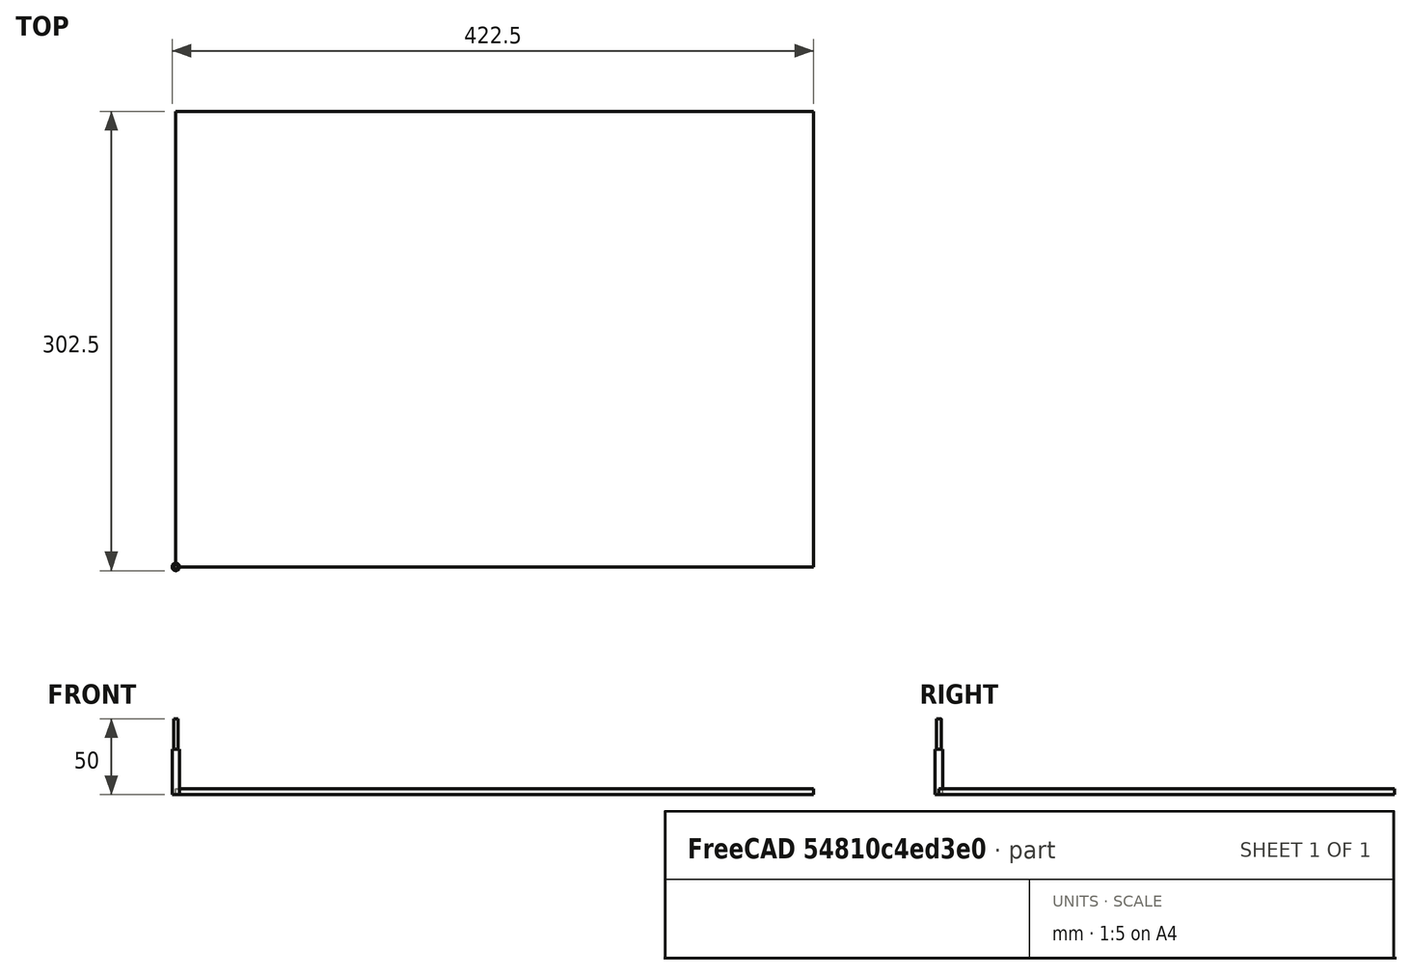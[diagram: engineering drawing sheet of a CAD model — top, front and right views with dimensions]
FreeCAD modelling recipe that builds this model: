
FCSTD DOCUMENT  (FreeCAD 0.21R33771 (Git))
Label: HousingAtari_Level_2_T01
License: All rights reserved
LicenseURL: https://en.wikipedia.org/wiki/All_rights_reserved
objects: Sketcher::SketchObject×7, Part::Part2DObjectPython×5, TechDraw::DrawViewDraft×4, Path::FeaturePython×3, App::DocumentObjectGroup×3, Part::FeaturePython×2, PartDesign::Body×1, App::FeaturePython×1, Mesh::FeaturePython×1, TechDraw::DrawSVGTemplate×1, TechDraw::DrawPage×1
note: 15 computed .brp shape members not serialized (recipe doc carries the construction recipe); baked Part::Feature solids carry a one-line shape summary decoded from their .brp

FEATURE [Sketcher::SketchObject] Sketch  label="A3"
  FullyConstrained = true
  MapMode = 5
  sketch-geometry (6):
    g0: LineSegment StartX=0 StartY=0 StartZ=0 EndX=420 EndY=0 EndZ=0
    g1: LineSegment StartX=420 StartY=0 StartZ=0 EndX=420 EndY=297 EndZ=0
    g2: LineSegment StartX=0 StartY=297 StartZ=0 EndX=0 EndY=0 EndZ=0
    g3: LineSegment StartX=0 StartY=297 StartZ=0 EndX=210 EndY=297 EndZ=0
    g4: LineSegment StartX=210 StartY=297 StartZ=0 EndX=420 EndY=297 EndZ=0
    g5: LineSegment StartX=210 StartY=297 StartZ=0 EndX=210 EndY=0 EndZ=0
  constraints (16):
    c: Coincident(g0,g1)
    c: Coincident(g2,g0)
    c: Horizontal(g0)
    c: Vertical(g1)
    c: Vertical(g2)
    c: Coincident(g0,g-1)
    c: DistanceX(g2,g1) = 420
    c: DistanceY(g2,g2) = 297
    c: Coincident(g3,g2)
    c: Horizontal(g3)
    c: Coincident(g4,g3)
    c: Coincident(g4,g1)
    c: Horizontal(g4)
    c: Equal(g4,g3)
    c: Coincident(g5,g3)
    c: Symmetric(g0,g0,g5)
FEATURE [Sketcher::SketchObject] Sketch001  label="BOX-OUTLINE"
  FullyConstrained = true
  MapMode = 5
  sketch-geometry (59):
    g0: LineSegment StartX=45 StartY=255 StartZ=0 EndX=45 EndY=220 EndZ=0
    g1: LineSegment StartX=45 StartY=220 StartZ=0 EndX=45 EndY=185 EndZ=0
    g2: LineSegment StartX=45 StartY=185 StartZ=0 EndX=110 EndY=185 EndZ=0
    g3: LineSegment StartX=110 StartY=185 StartZ=0 EndX=175 EndY=185 EndZ=0
    g4: LineSegment StartX=175 StartY=185 StartZ=0 EndX=175 EndY=220 EndZ=0
    g5: LineSegment StartX=175 StartY=220 StartZ=0 EndX=175 EndY=255 EndZ=0
    g6: LineSegment StartX=175 StartY=255 StartZ=0 EndX=110 EndY=255 EndZ=0
    g7: LineSegment StartX=110 StartY=255 StartZ=0 EndX=45 EndY=255 EndZ=0
    g8: LineSegment StartX=45 StartY=185 StartZ=0 EndX=0 EndY=0 EndZ=0
    g9: LineSegment StartX=45 StartY=185 StartZ=0 EndX=45 EndY=181 EndZ=0
    g10: LineSegment StartX=45 StartY=181 StartZ=0 EndX=175 EndY=181 EndZ=0
    g11: LineSegment StartX=175 StartY=181 StartZ=0 EndX=175 EndY=185 EndZ=0
    g12: LineSegment StartX=175 StartY=185 StartZ=0 EndX=171 EndY=185 EndZ=0
    g13: LineSegment StartX=171 StartY=185 StartZ=0 EndX=171 EndY=255 EndZ=0
    g14: LineSegment StartX=171 StartY=255 StartZ=0 EndX=175 EndY=255 EndZ=0
    g15: LineSegment StartX=175 StartY=255 StartZ=0 EndX=175 EndY=259 EndZ=0
    g16: LineSegment StartX=175 StartY=259 StartZ=0 EndX=45 EndY=259 EndZ=0
    g17: LineSegment StartX=45 StartY=259 StartZ=0 EndX=45 EndY=255 EndZ=0
    g18: LineSegment StartX=45 StartY=185 StartZ=0 EndX=49 EndY=185 EndZ=0
    g19: LineSegment StartX=49 StartY=185 StartZ=0 EndX=49 EndY=255 EndZ=0
    g20: LineSegment StartX=49 StartY=255 StartZ=0 EndX=45 EndY=255 EndZ=0
    g21: LineSegment StartX=45 StartY=181 StartZ=0 EndX=45 EndY=151 EndZ=0
    g22: LineSegment StartX=45 StartY=151 StartZ=0 EndX=175 EndY=151 EndZ=0
    g23: LineSegment StartX=175 StartY=151 StartZ=0 EndX=175 EndY=181 EndZ=0
    g24: LineSegment StartX=171 StartY=185 StartZ=0 EndX=205 EndY=185 EndZ=0
    g25: LineSegment StartX=205 StartY=185 StartZ=0 EndX=205 EndY=255 EndZ=0
    g26: LineSegment StartX=205 StartY=255 StartZ=0 EndX=171 EndY=255 EndZ=0
    g27: LineSegment StartX=175 StartY=259 StartZ=0 EndX=175 EndY=289 EndZ=0
    g28: LineSegment StartX=175 StartY=289 StartZ=0 EndX=45 EndY=289 EndZ=0
    g29: LineSegment StartX=45 StartY=289 StartZ=0 EndX=45 EndY=259 EndZ=0
    g30: LineSegment StartX=49 StartY=255 StartZ=0 EndX=15 EndY=255 EndZ=0
    g31: LineSegment StartX=15 StartY=255 StartZ=0 EndX=15 EndY=185 EndZ=0
    g32: LineSegment StartX=15 StartY=185 StartZ=0 EndX=49 EndY=185 EndZ=0
    g33: LineSegment StartX=175 StartY=151 StartZ=0 EndX=171 EndY=151 EndZ=0
    g34: LineSegment StartX=171 StartY=151 StartZ=0 EndX=171 EndY=185 EndZ=0
    g35: LineSegment StartX=175 StartY=181 StartZ=0 EndX=205 EndY=181 EndZ=0
    g36: LineSegment StartX=205 StartY=181 StartZ=0 EndX=205 EndY=185 EndZ=0
    g37: LineSegment StartX=175 StartY=259 StartZ=0 EndX=205 EndY=259 EndZ=0
    g38: LineSegment StartX=205 StartY=259 StartZ=0 EndX=205 EndY=255 EndZ=0
    g39: LineSegment StartX=171 StartY=255 StartZ=0 EndX=171 EndY=289 EndZ=0
    g40: LineSegment StartX=171 StartY=289 StartZ=0 EndX=175 EndY=289 EndZ=0
    g41: LineSegment StartX=45 StartY=289 StartZ=0 EndX=49 EndY=289 EndZ=0
    g42: LineSegment StartX=49 StartY=289 StartZ=0 EndX=49 EndY=255 EndZ=0
    g43: LineSegment StartX=15 StartY=255 StartZ=0 EndX=15 EndY=259 EndZ=0
    g44: LineSegment StartX=15 StartY=259 StartZ=0 EndX=45 EndY=259 EndZ=0
    g45: LineSegment StartX=15 StartY=185 StartZ=0 EndX=15 EndY=181 EndZ=0
    g46: LineSegment StartX=15 StartY=181 StartZ=0 EndX=45 EndY=181 EndZ=0
    g47: LineSegment StartX=49 StartY=185 StartZ=0 EndX=49 EndY=151 EndZ=0
    g48: LineSegment StartX=49 StartY=151 StartZ=0 EndX=45 EndY=151 EndZ=0
    g49: LineSegment StartX=45 StartY=151 StartZ=0 EndX=45 EndY=77 EndZ=0
    g50: LineSegment StartX=45 StartY=77 StartZ=0 EndX=175 EndY=77 EndZ=0
    g51: LineSegment StartX=175 StartY=77 StartZ=0 EndX=175 EndY=151 EndZ=0
    g52: LineSegment StartX=49 StartY=151 StartZ=0 EndX=49 EndY=81 EndZ=0
    g53: LineSegment StartX=49 StartY=81 StartZ=0 EndX=171 EndY=81 EndZ=0
    g54: LineSegment StartX=171 StartY=81 StartZ=0 EndX=171 EndY=151 EndZ=0
    g55: LineSegment StartX=49 StartY=155 StartZ=0 EndX=171 EndY=155 EndZ=0
    g56: LineSegment StartX=49 StartY=81 StartZ=0 EndX=49 EndY=77 EndZ=0
    g57: LineSegment StartX=171 StartY=81 StartZ=0 EndX=171 EndY=77 EndZ=0
    g58: LineSegment StartX=49 StartY=285 StartZ=0 EndX=171 EndY=285 EndZ=0
  constraints (162):
    c: Vertical(g0)
    c: Coincident(g1,g0)
    c: Vertical(g1)
    c: Coincident(g2,g1)
    c: Horizontal(g2)
    c: Coincident(g3,g2)
    c: Horizontal(g3)
    c: Coincident(g4,g3)
    c: Vertical(g4)
    c: Coincident(g5,g4)
    c: Vertical(g5)
    c: Horizontal(g6)
    c: Coincident(g7,g6)
    c: Coincident(g7,g0)
    c: Horizontal(g7)
    c: Vertical(g2,g6)
    c: Horizontal(g0,g4)
    c: Equal(g4,g5)
    c: Equal(g7,g6)
    c: Coincident(g5,g6)
    c: DistanceY(g1,g0) = 70
    c: DistanceX(g0,g5) = 130
    c: Coincident(g8,g1)
    c: Coincident(g8,g-1)
    c: DistanceX(g8,g8) = 45
    c: DistanceY(g8,g8) = 185
    c: Coincident(g9,g1)
    c: Vertical(g9)
    c: Coincident(g10,g9)
    c: Horizontal(g10)
    c: Coincident(g11,g10)
    c: Coincident(g11,g3)
    c: Vertical(g11)
    c: Coincident(g12,g3)
    c: Horizontal(g12)
    c: Coincident(g13,g12)
    c: Vertical(g13)
    c: Coincident(g14,g13)
    c: Coincident(g14,g5)
    c: Horizontal(g14)
    c: Equal(g11,g12)
    c: DistanceY(g11,g11) = 4
    c: Coincident(g15,g5)
    c: Vertical(g15)
    c: Coincident(g16,g15)
    c: Horizontal(g16)
    c: Coincident(g17,g16)
    c: Coincident(g17,g0)
    c: Vertical(g17)
    c: Equal(g14,g15)
    c: Coincident(g18,g1)
    c: Horizontal(g18)
    c: Coincident(g19,g18)
    c: Vertical(g19)
    c: Coincident(g20,g19)
    c: Coincident(g20,g0)
    c: Horizontal(g20)
    c: Equal(g17,g20)
    c: Coincident(g21,g9)
    c: Vertical(g21)
    c: Coincident(g22,g21)
    c: Horizontal(g22)
    c: Coincident(g23,g22)
    c: Coincident(g23,g10)
    c: Coincident(g24,g12)
    c: Horizontal(g24)
    c: Coincident(g25,g24)
    c: Vertical(g25)
    c: Coincident(g26,g25)
    c: Coincident(g26,g13)
    c: Horizontal(g26)
    c: Coincident(g27,g15)
    c: Vertical(g27)
    c: Coincident(g28,g27)
    c: Horizontal(g28)
    c: Coincident(g29,g28)
    c: Coincident(g29,g16)
    c: Coincident(g30,g19)
    c: Horizontal(g30)
    c: Coincident(g31,g30)
    c: Vertical(g31)
    c: Coincident(g32,g31)
    c: Coincident(g32,g18)
    c: Horizontal(g32)
    c: Vertical(g23)
    c: Coincident(g33,g22)
    c: Horizontal(g33)
    c: Coincident(g34,g33)
    c: Coincident(g34,g12)
    c: Vertical(g34)
    c: Coincident(g35,g10)
    c: Horizontal(g35)
    c: Coincident(g36,g35)
    c: Coincident(g36,g24)
    c: Coincident(g37,g15)
    c: Horizontal(g37)
    c: Coincident(g38,g37)
    c: Coincident(g38,g25)
    c: Coincident(g39,g13)
    c: Vertical(g39)
    c: Coincident(g40,g39)
    c: Coincident(g40,g27)
    c: Horizontal(g40)
    c: Coincident(g41,g28)
    c: Horizontal(g41)
    c: Coincident(g42,g41)
    c: Coincident(g42,g19)
    c: Coincident(g43,g30)
    c: Vertical(g43)
    c: Coincident(g44,g43)
    c: Coincident(g44,g16)
    c: Coincident(g45,g31)
    c: Vertical(g45)
    c: Coincident(g46,g45)
    c: Coincident(g46,g9)
    c: Horizontal(g46)
    c: Coincident(g47,g18)
    c: Coincident(g48,g47)
    c: Coincident(g48,g21)
    c: Vertical(g38)
    c: Vertical(g47)
    c: Vertical(g36)
    c: Horizontal(g44)
    c: Horizontal(g48)
    c: DistanceY(g16,g28) = 30
    c: Vertical(g42)
    c: Vertical(g29)
    c: DistanceY(g23,g23) = 30
    c: Distance(g44,g44) = 30
    c: DistanceX(g35,g35) = 30
    c: Coincident(g49,g21)
    c: Vertical(g49)
    c: Coincident(g50,g49)
    c: Horizontal(g50)
    c: Coincident(g51,g50)
    c: Coincident(g51,g22)
    c: Vertical(g51)
    c: Coincident(g52,g47)
    c: Vertical(g52)
    c: Coincident(g53,g52)
    c: Horizontal(g53)
    c: Coincident(g54,g53)
    c: Coincident(g54,g33)
    c: Vertical(g54)
    c: PointOnObject(g55,g47)
    c: PointOnObject(g55,g34)
    c: Horizontal(g55)
    c: DistanceY(g47,g55) = 4
    c: Coincident(g56,g52)
    c: PointOnObject(g56,g50)
    c: Vertical(g56)
    c: DistanceY(g56,g56) = 4
    c: DistanceY(g52,g52) = 70
    c: DistanceY(g35,g37) = 78
    c: Coincident(g57,g53)
    c: PointOnObject(g57,g50)
    c: Vertical(g57)
    c: DistanceY(g57,g55) = 78
    c: PointOnObject(g58,g42)
    c: PointOnObject(g58,g39)
    c: Horizontal(g58)
    c: DistanceY(g58,g39) = 4
FEATURE [PartDesign::Body] Body
  Group = -> [Sketch,Sketch001]
  Origin = -> Origin
FEATURE [Sketcher::SketchObject] Sketch002  label="CUT-BOX-BASE"
  ExternalGeometry = -> [Sketch001]
  FullyConstrained = false
  MapMode = 5
  sketch-geometry (30):
    g0: LineSegment StartX=45 StartY=220 StartZ=0 EndX=175 EndY=220 EndZ=0
    g1: LineSegment StartX=110 StartY=185 StartZ=0 EndX=110 EndY=255 EndZ=0
    g2: LineSegment StartX=49 StartY=205 StartZ=0 EndX=171 EndY=205 EndZ=0
    g3: LineSegment StartX=49 StartY=235 StartZ=0 EndX=171 EndY=235 EndZ=0
    g4: LineSegment StartX=83.7703 StartY=185 StartZ=0 EndX=83.7703 EndY=255 EndZ=0
    g5: LineSegment StartX=133.77 StartY=185 StartZ=0 EndX=133.77 EndY=255 EndZ=0
    g6: LineSegment StartX=49 StartY=205 StartZ=0 EndX=49 EndY=220 EndZ=0
    g7: LineSegment StartX=49 StartY=220 StartZ=0 EndX=49 EndY=235 EndZ=0
    g8: LineSegment StartX=171 StartY=205 StartZ=0 EndX=171 EndY=220 EndZ=0
    g9: LineSegment StartX=171 StartY=220 StartZ=0 EndX=171 EndY=235 EndZ=0
    g10: LineSegment StartX=171 StartY=205 StartZ=0 EndX=175 EndY=205 EndZ=0
    g11: LineSegment StartX=171 StartY=235 StartZ=0 EndX=175 EndY=235 EndZ=0
    g12: LineSegment StartX=49 StartY=235 StartZ=0 EndX=45 EndY=235 EndZ=0
    g13: LineSegment StartX=49 StartY=205 StartZ=0 EndX=45 EndY=205 EndZ=0
    g14: LineSegment StartX=83.7703 StartY=185 StartZ=0 EndX=110 EndY=185 EndZ=0
    g15: LineSegment StartX=110 StartY=185 StartZ=0 EndX=133.77 EndY=185 EndZ=0
    g16: LineSegment StartX=83.7703 StartY=185 StartZ=0 EndX=83.7703 EndY=181 EndZ=0
    g17: LineSegment StartX=133.77 StartY=185 StartZ=0 EndX=133.77 EndY=181 EndZ=0
    g18: LineSegment StartX=83.7703 StartY=255 StartZ=0 EndX=110 EndY=255 EndZ=0
    g19: LineSegment StartX=110 StartY=255 StartZ=0 EndX=133.77 EndY=255 EndZ=0
    g20: LineSegment StartX=133.77 StartY=255 StartZ=0 EndX=133.77 EndY=259 EndZ=0
    g21: LineSegment StartX=83.7703 StartY=255 StartZ=0 EndX=83.7703 EndY=259 EndZ=0
    g22: LineSegment StartX=45 StartY=205 StartZ=0 EndX=45 EndY=181 EndZ=0
    g23: LineSegment StartX=45 StartY=181 StartZ=0 EndX=83.7703 EndY=181 EndZ=0
    g24: LineSegment StartX=133.77 StartY=181 StartZ=0 EndX=175 EndY=181 EndZ=0
    g25: LineSegment StartX=175 StartY=181 StartZ=0 EndX=175 EndY=205 EndZ=0
    g26: LineSegment StartX=175 StartY=235 StartZ=0 EndX=175 EndY=259 EndZ=0
    g27: LineSegment StartX=175 StartY=259 StartZ=0 EndX=133.77 EndY=259 EndZ=0
    g28: LineSegment StartX=83.7703 StartY=259 StartZ=0 EndX=45 EndY=259 EndZ=0
    g29: LineSegment StartX=45 StartY=259 StartZ=0 EndX=45 EndY=235 EndZ=0
  constraints (75):
    c: Coincident(g0,g-4)
    c: Coincident(g0,g-6)
    c: Coincident(g1,g-10)
    c: PointOnObject(g3,g-11)
    c: PointOnObject(g4,g-10)
    c: PointOnObject(g2,g-9)
    c: PointOnObject(g3,g-9)
    c: Horizontal(g2)
    c: Vertical(g4)
    c: Vertical(g5)
    c: Horizontal(g3)
    c: PointOnObject(g2,g-11)
    c: PointOnObject(g5,g-13)
    c: Coincident(g1,g-13)
    c: PointOnObject(g4,g-12)
    c: Coincident(g6,g2)
    c: Symmetric(g-11,g-11,g6)
    c: Coincident(g7,g6)
    c: Coincident(g7,g3)
    c: Equal(g6,g7)
    c: DistanceY(g2,g3) = 30
    c: DistanceX(g4,g5) = 50
    c: Coincident(g8,g2)
    c: Symmetric(g-9,g-9,g8)
    c: Coincident(g9,g8)
    c: Coincident(g9,g3)
    c: Coincident(g10,g2)
    c: PointOnObject(g10,g-6)
    c: Horizontal(g10)
    c: Coincident(g11,g3)
    c: PointOnObject(g11,g-5)
    c: Horizontal(g11)
    c: Coincident(g12,g3)
    c: PointOnObject(g12,g-4)
    c: Horizontal(g12)
    c: Coincident(g13,g2)
    c: PointOnObject(g13,g-3)
    c: Horizontal(g13)
    c: Coincident(g14,g4)
    c: Coincident(g14,g1)
    c: Coincident(g15,g1)
    c: Coincident(g15,g5)
    c: Horizontal(g15)
    c: Coincident(g16,g4)
    c: PointOnObject(g16,g-7)
    c: Vertical(g16)
    c: Coincident(g17,g5)
    c: PointOnObject(g17,g-7)
    c: Vertical(g17)
    c: Coincident(g18,g4)
    c: Coincident(g18,g1)
    c: Coincident(g19,g1)
    c: Coincident(g19,g5)
    c: Coincident(g20,g5)
    c: PointOnObject(g20,g-14)
    c: Vertical(g20)
    c: Coincident(g21,g4)
    c: PointOnObject(g21,g-14)
    c: Vertical(g21)
    c: Coincident(g22,g13)
    c: Coincident(g22,g-7)
    c: Coincident(g23,g22)
    c: Coincident(g23,g16)
    c: Coincident(g24,g17)
    c: Coincident(g24,g-7)
    c: Coincident(g25,g24)
    c: Coincident(g25,g10)
    c: Coincident(g26,g11)
    c: Coincident(g26,g-14)
    c: Coincident(g27,g26)
    c: Coincident(g27,g20)
    c: Coincident(g28,g21)
    c: Coincident(g28,g-14)
    c: Coincident(g29,g28)
    c: Coincident(g29,g12)
FEATURE [App::FeaturePython] SetupSheet  # Path/CAM operation (typed FeaturePython)
  ClearanceHeightExpression = OpStockZMax+SetupSheet.ClearanceHeightOffset
  ClearanceHeightOffset = 5
  CoolantMode = 0
  CoolantModes = None | Flood | Mist
  FinalDepthExpression = OpFinalDepth
  HorizRapid = 0
  SafeHeightExpression = OpStockZMax+SetupSheet.SafeHeightOffset
  SafeHeightOffset = 3
  StartDepthExpression = OpStartDepth
  StepDownExpression = OpToolDiameter
  VertRapid = 0
FEATURE [Part::Part2DObjectPython] Clone2D  label="Model-CUT-BOX"  # Draft 2D object (typed FeaturePython)
  Fuse = false
  Objects = -> [Sketch002]
  PathResource = Model
  Scale = (1,1,1)
FEATURE [Part::FeaturePython] ToolBit  label="Endmill"  # Path/CAM toolbit (typed FeaturePython)
  BitPropertyNames = Chipload | CuttingEdgeHeight | Diameter | Flutes | Length | Material | ShankDiameter | SpindleDirection
  BitShape = <path>
  Chipload = 0
  CuttingEdgeHeight = 30
  Diameter = 5
  Flutes = 0
  Length = 50
  Material = 0
  ShankDiameter = 3
  ShapeName = endmill
  SpindleDirection = 0
FEATURE [Path::FeaturePython] TC__Default_Tool  label="TC: Default Tool"  # Path/CAM operation (typed FeaturePython)
  HorizFeed = 1000
  HorizRapid = 1000
  SpindleDir = 0
  SpindleSpeed = 1000
  Tool = -> ToolBit
  ToolNumber = 1
  VertFeed = 1000
  VertRapid = 1000
  expr: HorizRapid = 1000
  expr: VertRapid = 1000
FEATURE [App::DocumentObjectGroup] Tools
  Group = -> [TC__Default_Tool]
FEATURE [Path::FeaturePython] Engrave  # Path/CAM operation (typed FeaturePython)
  Active = true
  ClearanceHeight = 9
  CoolantMode = 0
  CycleTime = 00:00:03
  FinalDepth = -5
  OpFinalDepth = -5
  OpStartDepth = 0
  OpStockZMax = 4
  OpStockZMin = 0
  OpToolDiameter = 5
  SafeHeight = 7
  StartDepth = 0
  StartVertex = 0
  StepDown = 5
  ToolController = -> TC__Default_Tool
  expr: ClearanceHeight = OpStockZMax + SetupSheet.ClearanceHeightOffset
  expr: FinalDepth = OpFinalDepth
  expr: SafeHeight = OpStockZMax + SetupSheet.SafeHeightOffset
  expr: StartDepth = OpStartDepth
  expr: StepDown = OpToolDiameter
FEATURE [App::DocumentObjectGroup] Operations
  Group = -> [Engrave]
FEATURE [Part::FeaturePython] Stock001  # WARN: FeaturePython — macro-defined, semantics opaque (R4)
  Height = 4
  Length = 420
  StockType = CreateBox
  Width = 300
FEATURE [Mesh::FeaturePython] CutMaterial  # WARN: FeaturePython — macro-defined, semantics opaque (R4)
FEATURE [Sketcher::SketchObject] Sketch004  label="CUT-BOX-WALLS"
  ExternalGeometry = -> [Sketch002,Sketch001]
  FullyConstrained = false
  MapMode = 5
  sketch-geometry (32):
    g0: LineSegment StartX=45 StartY=259 StartZ=0 EndX=30 EndY=259 EndZ=0
    g1: LineSegment StartX=30 StartY=259 StartZ=0 EndX=30 EndY=255 EndZ=0
    g2: LineSegment StartX=30 StartY=255 StartZ=0 EndX=15 EndY=255 EndZ=0
    g3: LineSegment StartX=15 StartY=185 StartZ=0 EndX=30 EndY=185 EndZ=0
    g4: LineSegment StartX=30 StartY=185 StartZ=0 EndX=30 EndY=181 EndZ=0
    g5: LineSegment StartX=30 StartY=181 StartZ=0 EndX=45 EndY=181 EndZ=0
    g6: LineSegment StartX=175 StartY=181 StartZ=0 EndX=190 EndY=181 EndZ=0
    g7: LineSegment StartX=190 StartY=181 StartZ=0 EndX=190 EndY=185 EndZ=0
    g8: LineSegment StartX=190 StartY=185 StartZ=0 EndX=205 EndY=185 EndZ=0
    g9: LineSegment StartX=205 StartY=255 StartZ=0 EndX=190 EndY=255 EndZ=0
    g10: LineSegment StartX=190 StartY=255 StartZ=0 EndX=190 EndY=259 EndZ=0
    g11: LineSegment StartX=190 StartY=259 StartZ=0 EndX=175 EndY=259 EndZ=0
    g12: LineSegment StartX=30 StartY=185 StartZ=0 EndX=30 EndY=255 EndZ=0
    g13: LineSegment StartX=190 StartY=185 StartZ=0 EndX=190 EndY=255 EndZ=0
    g14: LineSegment StartX=15 StartY=220 StartZ=0 EndX=205 EndY=220 EndZ=0
    g15: LineSegment StartX=110 StartY=151 StartZ=0 EndX=110 EndY=289 EndZ=0
    g16: LineSegment StartX=15 StartY=255 StartZ=0 EndX=15 EndY=235 EndZ=0
    g17: LineSegment StartX=15 StartY=235 StartZ=0 EndX=20.6579 EndY=235 EndZ=0
    g18: LineSegment StartX=20.6579 StartY=235 StartZ=0 EndX=20.6579 EndY=205 EndZ=0
    g19: LineSegment StartX=20.6579 StartY=204.687 StartZ=0 EndX=15 EndY=204.687 EndZ=0
    g20: LineSegment StartX=15 StartY=204.687 StartZ=0 EndX=15 EndY=185 EndZ=0
    g21: LineSegment StartX=205 StartY=185 StartZ=0 EndX=205 EndY=205 EndZ=0
    g22: LineSegment StartX=205 StartY=205 StartZ=0 EndX=199.009 EndY=205 EndZ=0
    g23: LineSegment StartX=199.009 StartY=205 StartZ=0 EndX=199.009 EndY=235 EndZ=0
    g24: LineSegment StartX=199.009 StartY=235 StartZ=0 EndX=205 EndY=235 EndZ=0
    g25: LineSegment StartX=205 StartY=235 StartZ=0 EndX=205 EndY=255 EndZ=0
    g26: LineSegment StartX=20.6579 StartY=235 StartZ=0 EndX=45 EndY=235 EndZ=0
    g27: LineSegment StartX=49 StartY=235 StartZ=0 EndX=170.368 EndY=235 EndZ=0
    g28: LineSegment StartX=175 StartY=235 StartZ=0 EndX=199.009 EndY=235 EndZ=0
    g29: LineSegment StartX=22.3684 StartY=205 StartZ=0 EndX=45 EndY=205 EndZ=0
    g30: LineSegment StartX=49.8267 StartY=205 StartZ=0 EndX=171 EndY=205 EndZ=0
    g31: LineSegment StartX=175 StartY=205 StartZ=0 EndX=199.009 EndY=205 EndZ=0
  constraints (82):
    c: Coincident(g0,g-18)
    c: Horizontal(g0)
    c: Coincident(g1,g0)
    c: Vertical(g1)
    c: Coincident(g2,g1)
    c: Coincident(g2,g-20)
    c: Horizontal(g2)
    c: Horizontal(g3)
    c: Coincident(g4,g3)
    c: Vertical(g4)
    c: Coincident(g5,g4)
    c: Coincident(g5,g-7)
    c: Horizontal(g5)
    c: Coincident(g6,g-11)
    c: Horizontal(g6)
    c: Coincident(g7,g6)
    c: Vertical(g7)
    c: Coincident(g8,g7)
    c: Coincident(g8,g-21)
    c: Horizontal(g8)
    c: Horizontal(g9)
    c: Coincident(g10,g9)
    c: Vertical(g10)
    c: Coincident(g11,g10)
    c: Coincident(g11,g-15)
    c: Horizontal(g11)
    c: Coincident(g12,g3)
    c: Coincident(g12,g1)
    c: Vertical(g12)
    c: Coincident(g13,g7)
    c: Coincident(g13,g9)
    c: Vertical(g13)
    c: Equal(g2,g0)
    c: Equal(g9,g11)
    c: DistanceX(g2,g2) = 15
    c: Distance(g9,g9) = 15
    c: PointOnObject(g14,g-20)
    c: PointOnObject(g14,g-21)
    c: Horizontal(g14)
    c: Symmetric(g-22,g-22,g15)
    c: Symmetric(g-19,g-19,g15)
    c: PointOnObject(g-13,g14)
    c: Coincident(g16,g2)
    c: PointOnObject(g16,g-20)
    c: Coincident(g17,g16)
    c: Horizontal(g17)
    c: Coincident(g18,g17)
    c: Vertical(g18)
    c: PointOnObject(g19,g-20)
    c: Horizontal(g19)
    c: Coincident(g20,g19)
    c: Coincident(g20,g3)
    c: Vertical(g20)
    c: Coincident(g21,g8)
    c: PointOnObject(g21,g-21)
    c: Coincident(g22,g21)
    c: Horizontal(g22)
    c: Coincident(g23,g22)
    c: Vertical(g23)
    c: Coincident(g24,g23)
    c: PointOnObject(g24,g-21)
    c: Horizontal(g24)
    c: PointOnObject(g25,g-21)
    c: Coincident(g25,g9)
    c: Vertical(g25)
    c: Horizontal(g17,g-3)
    c: Horizontal(g18,g-6)
    c: Horizontal(g-11,g22)
    c: Horizontal(g-14,g23)
    c: Coincident(g26,g17)
    c: Coincident(g26,g-3)
    c: Coincident(g27,g-4)
    c: Horizontal(g27)
    c: Coincident(g28,g-14)
    c: Coincident(g28,g23)
    c: Coincident(g29,g-6)
    c: Horizontal(g29)
    c: Coincident(g30,g-12)
    c: Horizontal(g30)
    c: Coincident(g31,g-11)
    c: Coincident(g31,g22)
    c: PointOnObject(g25,g24)
FEATURE [Sketcher::SketchObject] Sketch005  label="CUT-BOX-WALS2"
  ExternalGeometry = -> [Sketch002,Sketch001]
  FullyConstrained = true
  MapMode = 5
  sketch-geometry (28):
    g0: LineSegment StartX=83.7703 StartY=181 StartZ=0 EndX=83.7703 EndY=151 EndZ=0
    g1: LineSegment StartX=133.77 StartY=181 StartZ=0 EndX=133.77 EndY=151 EndZ=0
    g2: LineSegment StartX=83.7703 StartY=151 StartZ=0 EndX=83.7703 EndY=155 EndZ=0
    g3: LineSegment StartX=83.7703 StartY=155 StartZ=0 EndX=133.77 EndY=155 EndZ=0
    g4: LineSegment StartX=133.77 StartY=155 StartZ=0 EndX=133.77 EndY=151 EndZ=0
    g5: LineSegment StartX=83.7703 StartY=259 StartZ=0 EndX=83.7703 EndY=289 EndZ=0
    g6: LineSegment StartX=133.77 StartY=259 StartZ=0 EndX=133.77 EndY=289 EndZ=0
    g7: LineSegment StartX=49 StartY=166 StartZ=0 EndX=171 EndY=166 EndZ=0
    g8: LineSegment StartX=45 StartY=166 StartZ=0 EndX=49 EndY=166 EndZ=0
    g9: LineSegment StartX=175 StartY=166 StartZ=0 EndX=171 EndY=166 EndZ=0
    g10: LineSegment StartX=175 StartY=274 StartZ=0 EndX=45 EndY=274 EndZ=0
    g11: LineSegment StartX=45 StartY=274 StartZ=0 EndX=49 EndY=274 EndZ=0
    g12: LineSegment StartX=175 StartY=274 StartZ=0 EndX=171 EndY=274 EndZ=0
    g13: LineSegment StartX=83.7703 StartY=289 StartZ=0 EndX=83.7703 EndY=285 EndZ=0
    g14: LineSegment StartX=83.7703 StartY=285 StartZ=0 EndX=133.77 EndY=285 EndZ=0
    g15: LineSegment StartX=133.77 StartY=285 StartZ=0 EndX=133.77 EndY=289 EndZ=0
    g16: LineSegment StartX=49 StartY=181 StartZ=0 EndX=49 EndY=166 EndZ=0
    g17: LineSegment StartX=45 StartY=166 StartZ=0 EndX=45 EndY=151 EndZ=0
    g18: LineSegment StartX=45 StartY=151 StartZ=0 EndX=83.7703 EndY=151 EndZ=0
    g19: LineSegment StartX=133.77 StartY=151 StartZ=0 EndX=175 EndY=151 EndZ=0
    g20: LineSegment StartX=175 StartY=151 StartZ=0 EndX=175 EndY=166 EndZ=0
    g21: LineSegment StartX=171 StartY=166 StartZ=0 EndX=171 EndY=181 EndZ=0
    g22: LineSegment StartX=49 StartY=259 StartZ=0 EndX=49 EndY=274 EndZ=0
    g23: LineSegment StartX=45 StartY=274 StartZ=0 EndX=45 EndY=289 EndZ=0
    g24: LineSegment StartX=45 StartY=289 StartZ=0 EndX=83.7703 EndY=289 EndZ=0
    g25: LineSegment StartX=133.77 StartY=289 StartZ=0 EndX=175 EndY=289 EndZ=0
    g26: LineSegment StartX=175 StartY=289 StartZ=0 EndX=175 EndY=274 EndZ=0
    g27: LineSegment StartX=171 StartY=274 StartZ=0 EndX=171 EndY=259 EndZ=0
  constraints (75):
    c: PointOnObject(g7,g-11)
    c: Coincident(g0,g-4)
    c: PointOnObject(g0,g-9)
    c: Vertical(g0)
    c: Coincident(g1,g-3)
    c: PointOnObject(g1,g-9)
    c: Vertical(g1)
    c: Coincident(g2,g0)
    c: PointOnObject(g2,g-10)
    c: Vertical(g2)
    c: Coincident(g3,g2)
    c: PointOnObject(g3,g-10)
    c: Coincident(g4,g3)
    c: Coincident(g4,g1)
    c: Vertical(g4)
    c: Coincident(g5,g-5)
    c: PointOnObject(g5,g-17)
    c: Vertical(g5)
    c: Coincident(g6,g-6)
    c: Vertical(g6)
    c: Horizontal(g7)
    c: PointOnObject(g7,g-8)
    c: PointOnObject(g8,g-7)
    c: Coincident(g8,g7)
    c: Horizontal(g8)
    c: Coincident(g9,g7)
    c: Horizontal(g9)
    c: Symmetric(g-13,g-13,g10)
    c: Symmetric(g-16,g-16,g10)
    c: Coincident(g11,g10)
    c: PointOnObject(g11,g10)
    c: Coincident(g12,g10)
    c: PointOnObject(g12,g10)
    c: PointOnObject(g6,g-17)
    c: Coincident(g13,g5)
    c: PointOnObject(g13,g5)
    c: Coincident(g14,g13)
    c: PointOnObject(g14,g6)
    c: Horizontal(g14)
    c: Coincident(g15,g14)
    c: Coincident(g15,g6)
    c: PointOnObject(g14,g-24)
    c: DistanceY(g9,g-20) = 15
    c: DistanceY(g-18,g10) = 15
    c: PointOnObject(g16,g-20)
    c: Coincident(g16,g7)
    c: Vertical(g16)
    c: Coincident(g17,g8)
    c: Coincident(g17,g-9)
    c: Coincident(g18,g17)
    c: Coincident(g18,g0)
    c: Coincident(g19,g1)
    c: Coincident(g19,g-12)
    c: Coincident(g20,g19)
    c: Coincident(g20,g9)
    c: Vertical(g20)
    c: Coincident(g21,g7)
    c: PointOnObject(g21,g-20)
    c: Vertical(g21)
    c: PointOnObject(g22,g-18)
    c: Coincident(g22,g11)
    c: Vertical(g22)
    c: Coincident(g23,g10)
    c: Coincident(g23,g-17)
    c: Coincident(g24,g23)
    c: Coincident(g24,g5)
    c: Coincident(g25,g6)
    c: Coincident(g25,g-17)
    c: Coincident(g26,g25)
    c: Coincident(g26,g10)
    c: Coincident(g27,g12)
    c: PointOnObject(g27,g-18)
    c: Vertical(g27)
    c: PointOnObject(g11,g-15)
    c: PointOnObject(g12,g-14)
FEATURE [Sketcher::SketchObject] Sketch006  label="CUT-ROOF"
  ExternalGeometry = -> [Sketch005,Sketch004,Sketch001]
  FullyConstrained = false
  MapMode = 2
  sketch-geometry (22):
    g0: LineSegment StartX=218.305 StartY=259 StartZ=0 EndX=218.305 EndY=181 EndZ=0
    g1: LineSegment StartX=190 StartY=181 StartZ=0 EndX=218.305 EndY=181 EndZ=0
    g2: LineSegment StartX=190 StartY=259 StartZ=0 EndX=218.305 EndY=259 EndZ=0
    g3: LineSegment StartX=49 StartY=151 StartZ=0 EndX=49 EndY=131 EndZ=0
    g4: LineSegment StartX=83.7703 StartY=151 StartZ=0 EndX=83.7703 EndY=77 EndZ=0
    g5: LineSegment StartX=133.77 StartY=151 StartZ=0 EndX=133.77 EndY=77 EndZ=0
    g6: LineSegment StartX=49 StartY=131 StartZ=0 EndX=171 EndY=131 EndZ=0
    g7: LineSegment StartX=49 StartY=101 StartZ=0 EndX=171 EndY=101 EndZ=0
    g8: LineSegment StartX=49 StartY=131 StartZ=0 EndX=45 EndY=131 EndZ=0
    g9: LineSegment StartX=45 StartY=131 StartZ=0 EndX=45 EndY=101 EndZ=0
    g10: LineSegment StartX=45 StartY=101 StartZ=0 EndX=49 EndY=101 EndZ=0
    g11: LineSegment StartX=49 StartY=101 StartZ=0 EndX=49 EndY=81 EndZ=0
    g12: LineSegment StartX=49 StartY=81 StartZ=0 EndX=83.7703 EndY=81 EndZ=0
    g13: LineSegment StartX=83.7703 StartY=81 StartZ=0 EndX=83.7703 EndY=77 EndZ=0
    g14: LineSegment StartX=83.7703 StartY=77 StartZ=0 EndX=133.77 EndY=77 EndZ=0
    g15: LineSegment StartX=133.77 StartY=77 StartZ=0 EndX=133.77 EndY=81 EndZ=0
    g16: LineSegment StartX=133.77 StartY=81 StartZ=0 EndX=171 EndY=81 EndZ=0
    g17: LineSegment StartX=171 StartY=81 StartZ=0 EndX=171 EndY=101 EndZ=0
    g18: LineSegment StartX=171 StartY=101 StartZ=0 EndX=175 EndY=101 EndZ=0
    g19: LineSegment StartX=175 StartY=101 StartZ=0 EndX=175 EndY=131 EndZ=0
    g20: LineSegment StartX=175 StartY=131 StartZ=0 EndX=171 EndY=131 EndZ=0
    g21: LineSegment StartX=171 StartY=131 StartZ=0 EndX=171 EndY=151 EndZ=0
  constraints (61):
    c: Vertical(g0)
    c: Coincident(g1,g-9)
    c: Coincident(g1,g0)
    c: Coincident(g2,g-8)
    c: Coincident(g2,g0)
    c: Horizontal(g2)
    c: Horizontal(g1)
    c: DistanceY(g0,g0) = 78
    c: Coincident(g3,g-10)
    c: PointOnObject(g3,g-10)
    c: Coincident(g4,g-3)
    c: PointOnObject(g4,g-12)
    c: Vertical(g4)
    c: Coincident(g5,g-5)
    c: PointOnObject(g5,g-12)
    c: Vertical(g5)
    c: Coincident(g6,g3)
    c: PointOnObject(g6,g-14)
    c: Horizontal(g6)
    c: PointOnObject(g7,g-10)
    c: PointOnObject(g7,g-14)
    c: Horizontal(g7)
    c: Coincident(g8,g3)
    c: PointOnObject(g8,g-11)
    c: Coincident(g9,g8)
    c: PointOnObject(g9,g-11)
    c: Coincident(g10,g9)
    c: Coincident(g10,g7)
    c: Coincident(g11,g7)
    c: Coincident(g11,g-13)
    c: Coincident(g12,g11)
    c: PointOnObject(g12,g4)
    c: Horizontal(g12)
    c: Coincident(g13,g12)
    c: Coincident(g13,g4)
    c: Coincident(g14,g4)
    c: Coincident(g14,g5)
    c: Coincident(g15,g5)
    c: PointOnObject(g15,g-13)
    c: Vertical(g15)
    c: Coincident(g16,g15)
    c: Coincident(g16,g-14)
    c: Coincident(g17,g16)
    c: Coincident(g17,g7)
    c: Coincident(g18,g7)
    c: PointOnObject(g18,g-15)
    c: Horizontal(g18)
    c: Coincident(g19,g18)
    c: PointOnObject(g19,g-15)
    c: Coincident(g20,g19)
    c: Coincident(g20,g6)
    c: Coincident(g21,g6)
    c: Coincident(g21,g-14)
    c: Horizontal(g20)
    c: Horizontal(g8)
    c: DistanceY(g21,g21) = 20
    c: DistanceY(g17,g17) = 20
    c: Horizontal(g10)
    c: DistanceY(g-17,g-17) = 30
    c: Distance(g19,g19) = 30
    c: DistanceY(g11,g3) = 70
FEATURE [Sketcher::SketchObject] Sketch003  label="CUT-Functional"
  ExternalGeometry = -> [Sketch006,Sketch002]
  FullyConstrained = false
  MapMode = 5
  sketch-geometry (29):
    g0: LineSegment StartX=49 StartY=151 StartZ=0 EndX=110 EndY=151 EndZ=0
    g1: LineSegment StartX=110 StartY=151 StartZ=0 EndX=171 EndY=151 EndZ=0
    g2: LineSegment StartX=171 StartY=131 StartZ=0 EndX=171 EndY=116 EndZ=0
    g3: LineSegment StartX=171 StartY=116 StartZ=0 EndX=171 EndY=101 EndZ=0
    g4: LineSegment StartX=110 StartY=141.519 StartZ=0 EndX=63.9482 EndY=141.519 EndZ=0
    g5: LineSegment StartX=110 StartY=141.519 StartZ=0 EndX=154.396 EndY=141.519 EndZ=0
    g6: LineSegment StartX=159.951 StartY=135.965 StartZ=0 EndX=159.951 EndY=116 EndZ=0
    g7: LineSegment StartX=159.951 StartY=116 StartZ=0 EndX=159.951 EndY=96.3153 EndZ=0
    g8: LineSegment StartX=154.396 StartY=90.7606 StartZ=0 EndX=63.7857 EndY=90.7606 EndZ=0
    g9: LineSegment StartX=59.5711 StartY=94.9753 StartZ=0 EndX=59.5711 EndY=137.142 EndZ=0
    g10: ArcOfCircle CenterX=63.9482 CenterY=137.142 CenterZ=0 NormalX=0 NormalY=0 NormalZ=1 AngleXU=0 Radius=4.3771 StartAngle=1.5708 EndAngle=3.14159
    g11: GeomPoint X=59.5711 Y=141.519 Z=0
    g12: ArcOfCircle CenterX=63.7857 CenterY=94.9753 CenterZ=0 NormalX=0 NormalY=0 NormalZ=1 AngleXU=0 Radius=4.21464 StartAngle=3.14159 EndAngle=4.71239
    g13: GeomPoint X=59.5711 Y=90.7606 Z=0
    g14: ArcOfCircle CenterX=154.396 CenterY=96.3153 CenterZ=0 NormalX=0 NormalY=0 NormalZ=1 AngleXU=0 Radius=5.55461 StartAngle=4.71239 EndAngle=6.28319
    g15: GeomPoint X=159.951 Y=90.7606 Z=0
    g16: ArcOfCircle CenterX=154.396 CenterY=135.965 CenterZ=0 NormalX=0 NormalY=0 NormalZ=1 AngleXU=0 Radius=5.55461 StartAngle=-9e-16 EndAngle=1.5708
    g17: GeomPoint X=159.951 Y=141.519 Z=0
    g18: LineSegment StartX=80 StartY=236.121 StartZ=0 EndX=110 EndY=236.121 EndZ=0
    g19: LineSegment StartX=110 StartY=236.121 StartZ=0 EndX=140 EndY=236.121 EndZ=0
    g20: Circle CenterX=80 CenterY=236.121 CenterZ=0 NormalX=0 NormalY=0 NormalZ=1 AngleXU=0 Radius=8
    g21: Circle CenterX=110 CenterY=236.121 CenterZ=0 NormalX=0 NormalY=0 NormalZ=1 AngleXU=0 Radius=8
    g22: Circle CenterX=140 CenterY=236.121 CenterZ=0 NormalX=0 NormalY=0 NormalZ=1 AngleXU=0 Radius=8
    g23: Circle CenterX=100 CenterY=199.619 CenterZ=0 NormalX=0 NormalY=0 NormalZ=1 AngleXU=0 Radius=1.5
    g24: Circle CenterX=110 CenterY=199.619 CenterZ=0 NormalX=0 NormalY=0 NormalZ=1 AngleXU=0 Radius=1.5
    g25: Circle CenterX=120 CenterY=199.619 CenterZ=0 NormalX=0 NormalY=0 NormalZ=1 AngleXU=0 Radius=1.5
    g26: LineSegment StartX=100 StartY=199.619 StartZ=0 EndX=110 EndY=199.619 EndZ=0
    g27: LineSegment StartX=110 StartY=199.619 StartZ=0 EndX=120 EndY=199.619 EndZ=0
    g28: Circle CenterX=33.9008 CenterY=220.697 CenterZ=0 NormalX=0 NormalY=0 NormalZ=1 AngleXU=0 Radius=8
  constraints (50):
    c: Coincident(g4,g5)
    c: Coincident(g6,g7)
    c: PointOnObject(g11,g9)
    c: PointOnObject(g11,g4)
    c: Tangent(g9,g10) = 1.5708
    c: Tangent(g4,g10) = -1.5708
    c: PointOnObject(g13,g9)
    c: PointOnObject(g13,g8)
    c: Tangent(g9,g12) = 1.5708
    c: Tangent(g8,g12) = 1.5708
    c: PointOnObject(g15,g8)
    c: PointOnObject(g15,g7)
    c: Tangent(g8,g14) = 1.5708
    c: Tangent(g7,g14) = 1.5708
    c: PointOnObject(g17,g6)
    c: PointOnObject(g17,g5)
    c: Tangent(g6,g16) = 1.5708
    c: Tangent(g5,g16) = 1.5708
    c: Vertical(g14,g16)
    c: Vertical(g6)
    c: Vertical(g7)
    c: Horizontal(g5)
    c: Horizontal(g4)
    c: Vertical(g9)
    c: Horizontal(g8)
    c: Horizontal(g18)
    c: Coincident(g19,g18)
    c: Horizontal(g19)
    c: Equal(g19,g18)
    c: Vertical(g18,g-6)
    c: Coincident(g20,g18)
    c: Coincident(g21,g18)
    c: Coincident(g22,g19)
    c: Equal(g22,g21)
    c: Equal(g21,g20)
    c: Diameter(g22) = 16
    c: DistanceX(g19,g19) = 30
    c: Equal(g25,g24)
    c: Equal(g24,g23)
    c: Diameter(g25) = 3
    c: Coincident(g26,g23)
    c: Coincident(g26,g24)
    c: Horizontal(g26)
    c: Coincident(g27,g24)
    c: Coincident(g27,g25)
    c: Horizontal(g27)
    c: Equal(g26,g27)
    c: DistanceX(g27,g27) = 10
    c: Vertical(g24,g21)
    c: Diameter(g28) = 16
FEATURE [Part::Part2DObjectPython] Clone2D001  label="Model-CUT-Functional"  # Draft 2D object (typed FeaturePython)
  Fuse = false
  Objects = -> [Sketch003]
  PathResource = Model
  Scale = (1,1,1)
FEATURE [Part::Part2DObjectPython] Clone2D002  label="Model-CUT-BOX-WALLS"  # Draft 2D object (typed FeaturePython)
  Fuse = false
  Objects = -> [Sketch004]
  PathResource = Model
  Scale = (1,1,1)
FEATURE [Part::Part2DObjectPython] Clone2D003  label="Model-CUT-BOX-WALS2"  # Draft 2D object (typed FeaturePython)
  Fuse = false
  Objects = -> [Sketch005]
  PathResource = Model
  Scale = (1,1,1)
FEATURE [Part::Part2DObjectPython] Clone2D004  label="Model-CUT-ROOF"  # Draft 2D object (typed FeaturePython)
  Fuse = false
  Objects = -> [Sketch006]
  PathResource = Model
  Scale = (1,1,1)
FEATURE [App::DocumentObjectGroup] Model
  Group = -> [Clone2D,Clone2D001,Clone2D002,Clone2D003,Clone2D004]
FEATURE [Path::FeaturePython] Job  # Path/CAM operation (typed FeaturePython)
  CycleTime = 00:00:03
  Fixtures = G54
  GeometryTolerance = 0.01
  Group = -> [Sketch005]
  JobType = 0
  Model = -> Model
  Operations = -> Operations
  OrderOutputBy = 0
  PostProcessor = 10
  PostProcessorOutputFile = <userpath>/Documents/AdruinoAtariPaddle/FREECAD/HousingAtari_RAW.nc
  SetupSheet = -> SetupSheet
  SplitOutput = false
  Stock = -> Stock001
  Tools = -> Tools
FEATURE [TechDraw::DrawSVGTemplate] Template
  Height = 210
  Orientation = 1
  Template = <path>
  Width = 297
FEATURE [TechDraw::DrawViewDraft] DraftView001
  Direction = (0,0,1)
  FontSize = 12
  LineSpacing = 1
  LineStyle = Solid
  LineWidth = 0.35
  LockPosition = false
  OverrideStyle = false
  Rotation = 0
  Scale = 0.6
  ScaleType = 2
  Source = -> Sketch006
  Symbol = <svg\n	xmlns="http://www.w3.org/2000/svg" version="1.1"\n	xmlns:freecad="http://www.freecad.org/wiki/index.php?title=Svg_Namespace">\n<g transform ="scale(1,-1)">\n    <path id="Sketch006_w0000"  d="M 49.0 151.0 L 49.0 131.0 L 45.0 131.0 L 45.0 101.0 L 49.0 101.0 L 49.0 81.0 L 83.7703438155425 81.0 L 83.7703438155425 77.0 L 133.7703438155425 77.00000000000001 L 133.7703438155425 81.00000000000001 L 171.0 81.00000000000001 L 171.0 101.00000000000001 L 175.0 101.00000000000001 L 175.0 131.0 L 171.0 131.0 L 171.0 151.0 " stroke="#000000" stroke-width="1.1666666666666667 px" style="stroke-width:1.1666666666666667;stroke-miterlimit:4;stroke-dasharray:none;stroke-linecap:square;fill:none;fill-opacity:1;fill-rule: evenodd"/>\n</g>\n\n</svg>
  X = 147.769
  Y = 49.2811
FEATURE [TechDraw::DrawViewDraft] DraftView002
  Direction = (0,0,1)
  FontSize = 12
  LineSpacing = 1
  LineStyle = Solid
  LineWidth = 0.35
  LockPosition = false
  OverrideStyle = false
  Rotation = 0
  Scale = 0.6
  ScaleType = 2
  Source = -> Sketch005
  Symbol = <svg\n	xmlns="http://www.w3.org/2000/svg" version="1.1"\n	xmlns:freecad="http://www.freecad.org/wiki/index.php?title=Svg_Namespace">\n<g transform ="scale(1,-1)">\n    <path id="Sketch005_w0000"  d="M 48.99999999999998 181.0 L 48.99999999999998 166.0 L 45.0 166.0 L 45.0 151.0 L 83.7703438155425 151.0 L 83.7703438155425 155.0 L 133.7703438155425 155.0 L 133.7703438155425 151.0 L 175.0 151.0 L 175.0 166.0 L 171.0 166.0 L 171.0 181.0 " stroke="#000000" stroke-width="1.1666666666666667 px" style="stroke-width:1.1666666666666667;stroke-miterlimit:4;stroke-dasharray:none;stroke-linecap:square;fill:none;fill-opacity:1;fill-rule: evenodd"/>\n<path id="Sketch005_w0001"  d="M 48.99999999999997 259.0 L 48.99999999999997 274.0 L 45.0 274.0 L 45.0 289.0 L 83.7703438155425 289.0 L 83.7703438155425 285.0 L 133.77034381554242 285.0 L 133.7703438155425 289.0 L 175.0 289.0 L 175.0 274.0 L 171.0 274.0 L 171.0 259.0 " stroke="#000000" stroke-width="1.1666666666666667 px" style="stroke-width:1.1666666666666667;stroke-miterlimit:4;stroke-dasharray:none;stroke-linecap:square;fill:none;fill-opacity:1;fill-rule: evenodd"/>\n</g>\n\n</svg>
  X = 147.769
  Y = 113.527
FEATURE [TechDraw::DrawViewDraft] DraftView003
  Direction = (0,0,1)
  FontSize = 12
  LineSpacing = 1
  LineStyle = Solid
  LineWidth = 0.35
  LockPosition = false
  OverrideStyle = false
  Rotation = 0
  Scale = 0.6
  ScaleType = 2
  Source = -> Sketch004
  Symbol = <svg\n	xmlns="http://www.w3.org/2000/svg" version="1.1"\n	xmlns:freecad="http://www.freecad.org/wiki/index.php?title=Svg_Namespace">\n<g transform ="scale(1,-1)">\n    <path id="Sketch004_w0000"  d="M 45.0 259.0 L 30.0 259.0 L 30.0 255.0 L 14.999999999999998 255.0 L 15.0 235.0 L 20.657879 235.0 L 20.657879 205.0 " stroke="#000000" stroke-width="1.1666666666666667 px" style="stroke-width:1.1666666666666667;stroke-miterlimit:4;stroke-dasharray:none;stroke-linecap:square;fill:none;fill-opacity:1;fill-rule: evenodd"/>\n<path id="Sketch004_w0001"  d="M 20.657879 204.687439 L 15.0 204.687439 L 15.0 185.0 L 30.0 185.0 L 30.0 181.0 L 45.0 181.0 " stroke="#000000" stroke-width="1.1666666666666667 px" style="stroke-width:1.1666666666666667;stroke-miterlimit:4;stroke-dasharray:none;stroke-linecap:square;fill:none;fill-opacity:1;fill-rule: evenodd"/>\n<path id="Sketch004_w0002"  d="M 175.0 181.0 L 190.0 181.0 L 190.0 185.0 L 205.0 185.0 L 205.0 205.0 L 199.0094149999999 205.0 L 199.0094149999999 235.0 L 205.0 234.99999999999974 L 205.0 255.0 L 190.0 255.0 L 190.0 259.0 L 175.0 259.0 " stroke="#000000" stroke-width="1.1666666666666667 px" style="stroke-width:1.1666666666666667;stroke-miterlimit:4;stroke-dasharray:none;stroke-linecap:square;fill:none;fill-opacity:1;fill-rule: evenodd"/>\n</g>\n\n</svg>
  X = 147.769
  Y = 114.014
FEATURE [TechDraw::DrawViewDraft] DraftView004
  Direction = (0,0,1)
  FontSize = 12
  LineSpacing = 1
  LineStyle = Solid
  LineWidth = 0.35
  LockPosition = false
  OverrideStyle = false
  Rotation = 0
  Scale = 0.6
  ScaleType = 2
  Source = -> Sketch002
  Symbol = <svg\n	xmlns="http://www.w3.org/2000/svg" version="1.1"\n	xmlns:freecad="http://www.freecad.org/wiki/index.php?title=Svg_Namespace">\n<g transform ="scale(1,-1)">\n    <path id="Sketch002_w0000"  d="M 45.0 181.0 L 83.7703438155425 181.0 L 83.7703438155425 185.00000000000003 L 110.0 185.0 L 133.7703438155425 185.0 L 133.7703438155425 181.0 L 175.0 181.0 L 175.0 205.0 L 171.0 205.0 L 171.0 220.0 L 171.0 235.0 L 175.0 235.0 L 175.0 259.0 L 133.7703438155425 259.0 L 133.7703438155425 255.0 L 110.0 255.0 L 83.7703438155425 255.0 L 83.7703438155425 259.0 L 45.0 259.0 L 45.0 235.0 L 49.0 235.0 L 49.0 220.0 L 49.0 205.0 L 45.0 205.0 L 45.0 181.0 " stroke="#000000" stroke-width="1.1666666666666667 px" style="stroke-width:1.1666666666666667;stroke-miterlimit:4;stroke-dasharray:none;stroke-linecap:square;fill:none;fill-opacity:1;fill-rule: evenodd"/>\n</g>\n\n</svg>
  X = 147.769
  Y = 114.014
FEATURE [TechDraw::DrawPage] Page
  KeepUpdated = true
  NextBalloonIndex = 1
  ProjectionType = 0
  Scale = 0.6
  Template = -> Template
  Views = -> [DraftView001,DraftView002,DraftView003,DraftView004]
note: 2 file-system paths scrubbed to <path> (originals preserved in the JSON sidecar)
